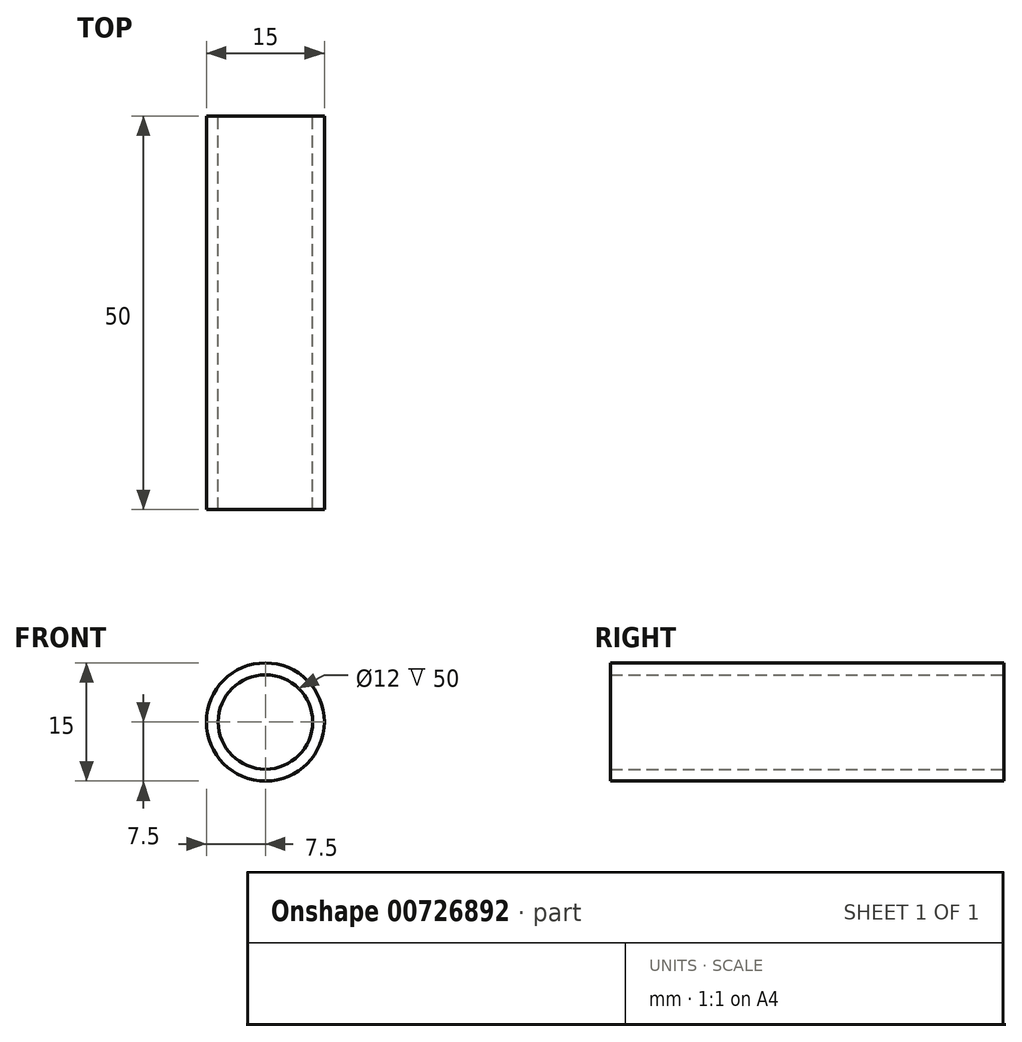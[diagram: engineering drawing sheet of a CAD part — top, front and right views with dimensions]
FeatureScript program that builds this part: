
annotation { "Feature Type Name" : "Feature", "Feature Type Description" : "" }
export const myFeature = defineFeature(function(context is Context, id is Id, definition is map)
    precondition{}
    {
        {
            var Q0;
            Q0=qCreatedBy(makeId("Front.planeOp"),FACE);
            var sketch = newSketch(context, id + "F0", { "sketchPlane" : qUnion([Q0])});
            skCircle(sketch, "E0", {"center": v(0, 0) * mm, "radius": 6 * mm});
            skCircle(sketch, "E1", {"center": v(0, 0) * mm, "radius": 7.5 * mm});
            skSolve(sketch);
        }
        {
            var Q0;
            Q0 = qSketchRegion(id + "F0", true);
            extrude(context, id + "F1", {"entities" : qUnion([Q0]), "depth" : 50 * mm, "offsetDistance" : 25 * mm});
        }
    });
